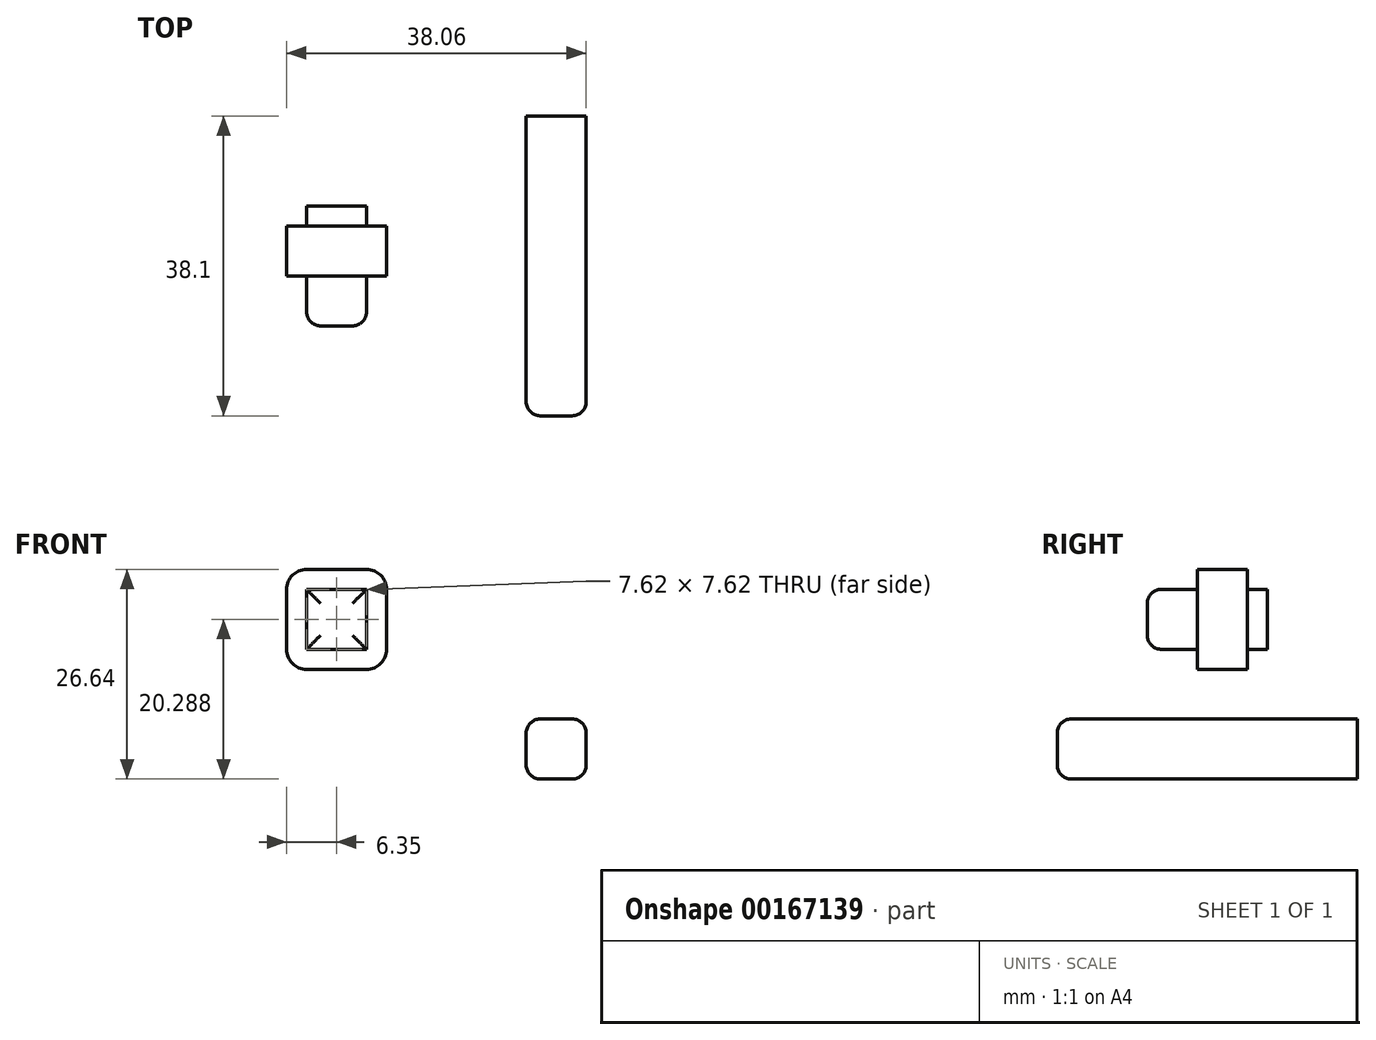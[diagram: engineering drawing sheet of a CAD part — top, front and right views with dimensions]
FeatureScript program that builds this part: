
annotation { "Feature Type Name" : "Feature", "Feature Type Description" : "" }
export const myFeature = defineFeature(function(context is Context, id is Id, definition is map)
    precondition{}
    {
        {
            var Q0;
            Q0=qCreatedBy(makeId("Top.planeOp"),FACE);
            var sketch = newSketch(context, id + "F0", { "sketchPlane" : qUnion([Q0])});
            skLineSegment(sketch, "E0.bottom", {"start": v(3.81, 19.05) * mm, "end": v(-3.81, 19.05) * mm});
            skLineSegment(sketch, "E0.top", {"start": v(3.8, -19.05) * mm, "end": v(-3.81, -19.05) * mm});
            skLineSegment(sketch, "E0.left", {"start": v(3.8, 19.05) * mm, "end": v(3.8, -19.05) * mm});
            skLineSegment(sketch, "E0.right", {"start": v(-3.81, 19.05) * mm, "end": v(-3.81, -19.05) * mm});
            skPoint(sketch, "E0.middle", {"position": v(0, 0) * mm});
            skLineSegment(sketch, "E1", {"start": v(0, 0) * mm, "end": v(0, 19.05) * mm});
            skLineSegment(sketch, "E2", {"start": v(0, 19.05) * mm, "end": v(0, -19.05) * mm});
            skSolve(sketch);
        }
        {
            var Q0;
            {var subQ4=sQuery(id+"F0.wireOp",EDGE,"E0.right");Q0=makeQuery(id+"F0.imprint","IMPRINT",FACE,{"disambiguationData":[TD([[makeQuery(id+"F0.imprint","IMPRINT",EDGE,{"derivedFrom":subQ4}),1.0]])]});}
            var Q1;
            {var subQ4=sQuery(id+"F0.wireOp",EDGE,"E0.left");Q1=makeQuery(id+"F0.imprint","IMPRINT",FACE,{"disambiguationData":[TD([[makeQuery(id+"F0.imprint","IMPRINT",EDGE,{"derivedFrom":subQ4}),-1.0]])]});}
            extrude(context, id + "F1", {"entities" : qUnion([Q0, Q1]), "depth" : 7.62 * mm});
        }
        {
            var Q0;
            Q0=makeQuery(id+"F1.opExtrude","CAP_EDGE",EDGE,{"disambiguationData":[OSD([sQuery(id+"F0.wireOp",EDGE,"E0.right")])],"isStart":false});
            var Q1;
            Q1=makeQuery(id+"F1.opExtrude","CAP_EDGE",EDGE,{"disambiguationData":[OSD([sQuery(id+"F0.wireOp",EDGE,"E0.right")])],"isStart":true});
            var Q2;
            Q2=makeQuery(id+"F1.opExtrude","CAP_EDGE",EDGE,{"disambiguationData":[OSD([sQuery(id+"F0.wireOp",EDGE,"E0.left")])],"isStart":false});
            var Q3;
            Q3=makeQuery(id+"F1.opExtrude","CAP_EDGE",EDGE,{"disambiguationData":[OSD([sQuery(id+"F0.wireOp",EDGE,"E0.left")])],"isStart":true});
            var Q4;
            Q4=makeQuery(id+"F1.opExtrude","SWEPT_EDGE",EDGE,{"disambiguationData":[OSD([sQuery(id+"F0.wireOp",EDGE,"E0.top"),sQuery(id+"F0.wireOp",EDGE,"E0.right")])]});
            var Q5;
            Q5=makeQuery(id+"F1.opExtrude","CAP_EDGE",EDGE,{"disambiguationData":[OSD([sQuery(id+"F0.wireOp",EDGE,"E0.top")])],"isStart":true});
            var Q6;
            Q6=makeQuery(id+"F1.opExtrude","CAP_EDGE",EDGE,{"disambiguationData":[OSD([sQuery(id+"F0.wireOp",EDGE,"E0.top")])],"isStart":false});
            var Q7;
            Q7=makeQuery(id+"F1.opExtrude","SWEPT_EDGE",EDGE,{"disambiguationData":[OSD([sQuery(id+"F0.wireOp",EDGE,"E0.top"),sQuery(id+"F0.wireOp",EDGE,"E0.left")])]});
            fillet(context, id + "F2", {"entities" : qUnion([Q0, Q1, Q2, Q3, Q4, Q5, Q6, Q7]), "radius" : 1.78 * mm, "tangentPropagation" : true, "allowEdgeOverflow" : false});
        }
        {
            var Q0;
            Q0=qCreatedBy(makeId("Front.planeOp"),FACE);
            var sketch = newSketch(context, id + "F3", { "sketchPlane" : qUnion([Q0])});
            skLineSegment(sketch, "E3.bottom", {"start": v(-24.09, 24.1) * mm, "end": v(-31.7, 24.1) * mm});
            skLineSegment(sketch, "E3.top", {"start": v(-24.09, 16.48) * mm, "end": v(-31.7, 16.48) * mm});
            skLineSegment(sketch, "E3.left", {"start": v(-24.09, 24.1) * mm, "end": v(-24.09, 16.48) * mm});
            skLineSegment(sketch, "E3.right", {"start": v(-31.7, 24.1) * mm, "end": v(-31.7, 16.48) * mm});
            skPoint(sketch, "E3.middle", {"position": v(-27.9, 20.29) * mm});
            skLineSegment(sketch, "E4.bottom", {"start": v(-21.55, 26.64) * mm, "end": v(-34.25, 26.64) * mm});
            skLineSegment(sketch, "E4.top", {"start": v(-21.55, 13.94) * mm, "end": v(-34.25, 13.94) * mm});
            skLineSegment(sketch, "E4.left", {"start": v(-21.55, 26.64) * mm, "end": v(-21.55, 13.94) * mm});
            skLineSegment(sketch, "E4.right", {"start": v(-34.25, 26.64) * mm, "end": v(-34.25, 13.94) * mm});
            skSolve(sketch);
        }
        {
            var Q0;
            Q0=makeQuery(id+"F3.imprint","IMPRINT",FACE,{"disambiguationData":[TD([[makeQuery(id+"F3.imprint","IMPRINT",EDGE,{"derivedFrom":sQuery(id+"F3.wireOp",EDGE,"E3.bottom")}),1.0]])]});
            extrude(context, id + "F4", {"entities" : qUnion([Q0]), "depth" : 15.24 * mm, "symmetric" : true});
        }
        {
            var Q0;
            Q0=makeQuery(id+"F3.imprint","IMPRINT",FACE,{"disambiguationData":[TD([[makeQuery(id+"F3.imprint","IMPRINT",EDGE,{"derivedFrom":sQuery(id+"F3.wireOp",EDGE,"E3.bottom")}),-1.0]])]});
            var Q1;
            Q1=makeQuery(id+"F4.opExtrude","CAP_FACE",FACE,{"disambiguationData":[OSD([sQuery(id+"F3.wireOp",EDGE,"E3.bottom"),sQuery(id+"F3.wireOp",EDGE,"E3.top"),sQuery(id+"F3.wireOp",EDGE,"E3.left"),sQuery(id+"F3.wireOp",EDGE,"E3.right")])],"isStart":false});
            var Q2;
            Q2=makeQuery(id+"F4.opExtrude","SWEPT_BODY",BODY,{"disambiguationData":[OSD([sQuery(id+"F3.wireOp",EDGE,"E3.bottom"),sQuery(id+"F3.wireOp",EDGE,"E3.top"),sQuery(id+"F3.wireOp",EDGE,"E3.left"),sQuery(id+"F3.wireOp",EDGE,"E3.right")])]});
            extrude(context, id + "F5", {"entities" : qUnion([Q0]), "operationType" : NewBodyOperationType.ADD, "oppositeDirection" : true, "endBoundEntityFace" : qUnion([Q1]), "endBoundEntityBody" : qUnion([Q2]), "depth" : 5.08 * mm, "hasSecondDirection" : true, "secondDirectionOppositeDirection" : false, "secondDirectionDepth" : 1.27 * mm});
        }
        {
            var Q0;
            Q0=makeQuery(id+"F5.opExtrude","SWEPT_EDGE",EDGE,{"disambiguationData":[OSD([sQuery(id+"F3.wireOp",EDGE,"E4.bottom"),sQuery(id+"F3.wireOp",EDGE,"E4.right")])]});
            var Q1;
            Q1=makeQuery(id+"F5.opExtrude","SWEPT_EDGE",EDGE,{"disambiguationData":[OSD([sQuery(id+"F3.wireOp",EDGE,"E4.bottom"),sQuery(id+"F3.wireOp",EDGE,"E4.left")])]});
            var Q2;
            Q2=makeQuery(id+"F5.opExtrude","SWEPT_EDGE",EDGE,{"disambiguationData":[OSD([sQuery(id+"F3.wireOp",EDGE,"E4.top"),sQuery(id+"F3.wireOp",EDGE,"E4.right")])]});
            var Q3;
            Q3=makeQuery(id+"F5.opExtrude","SWEPT_EDGE",EDGE,{"disambiguationData":[OSD([sQuery(id+"F3.wireOp",EDGE,"E4.top"),sQuery(id+"F3.wireOp",EDGE,"E4.left")])]});
            fillet(context, id + "F6", {"entities" : qUnion([Q0, Q1, Q2, Q3]), "radius" : 2.54 * mm, "tangentPropagation" : true, "allowEdgeOverflow" : false});
        }
        {
            var Q0;
            Q0=makeQuery(id+"F4.opExtrude","CAP_EDGE",EDGE,{"disambiguationData":[OSD([sQuery(id+"F3.wireOp",EDGE,"E3.left")])],"isStart":false});
            var Q1;
            Q1=makeQuery(id+"F4.opExtrude","CAP_EDGE",EDGE,{"disambiguationData":[OSD([sQuery(id+"F3.wireOp",EDGE,"E3.right")])],"isStart":false});
            var Q2;
            Q2=makeQuery(id+"F4.opExtrude","CAP_EDGE",EDGE,{"disambiguationData":[OSD([sQuery(id+"F3.wireOp",EDGE,"E3.top")])],"isStart":false});
            var Q3;
            Q3=makeQuery(id+"F4.opExtrude","CAP_EDGE",EDGE,{"disambiguationData":[OSD([sQuery(id+"F3.wireOp",EDGE,"E3.bottom")])],"isStart":false});
            fillet(context, id + "F7", {"entities" : qUnion([Q0, Q1, Q2, Q3]), "radius" : 1.78 * mm, "tangentPropagation" : true, "allowEdgeOverflow" : false});
        }
    });
